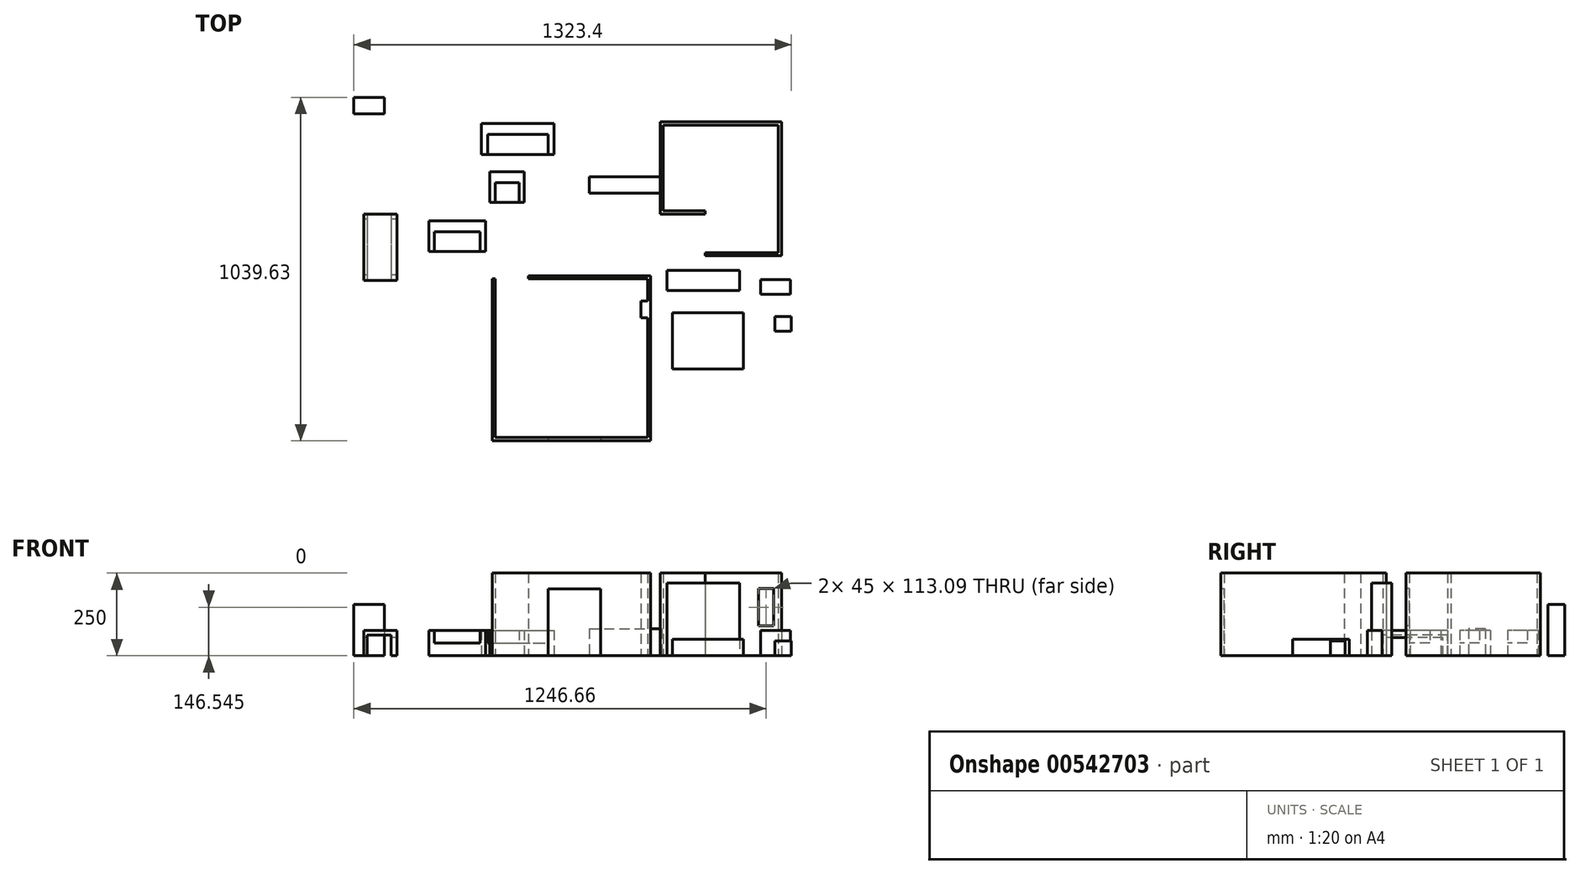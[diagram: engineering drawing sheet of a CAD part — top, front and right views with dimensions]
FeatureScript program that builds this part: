
annotation { "Feature Type Name" : "Feature", "Feature Type Description" : "" }
export const myFeature = defineFeature(function(context is Context, id is Id, definition is map)
    precondition{}
    {
        {
            var Q0;
            Q0=qCreatedBy(makeId("Top.planeOp"),FACE);
            var sketch = newSketch(context, id + "F0", { "sketchPlane" : qUnion([Q0])});
            skLineSegment(sketch, "E0", {"start": v(-41.59, 0) * mm, "end": v(-177.59, 0) * mm});
            skLineSegment(sketch, "E1", {"start": v(-177.59, 0) * mm, "end": v(-177.59, 280) * mm});
            skLineSegment(sketch, "E2", {"start": v(-177.59, 280) * mm, "end": v(190.41, 280) * mm});
            skLineSegment(sketch, "E3", {"start": v(190.41, 280) * mm, "end": v(190.41, -126) * mm});
            skLineSegment(sketch, "E4", {"start": v(190.41, -126) * mm, "end": v(-41.59, -126) * mm});
            skLineSegment(sketch, "E5", {"start": v(-41.59, -126) * mm, "end": v(-41.59, -101) * mm});
            skLineSegment(sketch, "E6", {"start": v(-41.59, -101) * mm, "end": v(-41.59, -101) * mm});
            skLineSegment(sketch, "E7", {"start": v(-41.59, -101) * mm, "end": v(-51.59, -101) * mm});
            skLineSegment(sketch, "E8", {"start": v(-41.59, -101) * mm, "end": v(-41.59, -116) * mm});
            skLineSegment(sketch, "E9", {"start": v(-41.59, -116) * mm, "end": v(180.41, -116) * mm});
            skLineSegment(sketch, "E10", {"start": v(180.41, -116) * mm, "end": v(180.41, 270) * mm});
            skLineSegment(sketch, "E11", {"start": v(180.41, 270) * mm, "end": v(-167.59, 270) * mm});
            skLineSegment(sketch, "E12", {"start": v(-167.59, 270) * mm, "end": v(-167.59, 10) * mm});
            skLineSegment(sketch, "E13", {"start": v(-167.59, 10) * mm, "end": v(-41.59, 10) * mm});
            skLineSegment(sketch, "E14", {"start": v(-41.59, 10) * mm, "end": v(-41.59, 0) * mm});
            skLineSegment(sketch, "E15", {"start": v(-51.59, -101) * mm, "end": v(-51.59, -126) * mm});
            skLineSegment(sketch, "E16", {"start": v(-51.59, -126) * mm, "end": v(-41.59, -126) * mm});
            skLineSegment(sketch, "E17", {"start": v(-575.48, -196) * mm, "end": v(-215.52, -196) * mm});
            skLineSegment(sketch, "E18", {"start": v(-215.52, -196) * mm, "end": v(-215.48, -263) * mm});
            skLineSegment(sketch, "E19", {"start": v(-215.48, -263) * mm, "end": v(-235.48, -263) * mm});
            skLineSegment(sketch, "E20", {"start": v(-235.48, -263) * mm, "end": v(-235.48, -313) * mm});
            skLineSegment(sketch, "E21", {"start": v(-235.48, -313) * mm, "end": v(-215.48, -313) * mm});
            skLineSegment(sketch, "E22", {"start": v(-215.48, -313) * mm, "end": v(-215.48, -676) * mm});
            skLineSegment(sketch, "E23", {"start": v(-215.48, -676) * mm, "end": v(-675.48, -676) * mm});
            skLineSegment(sketch, "E24", {"start": v(-675.48, -676) * mm, "end": v(-675.48, -196) * mm});
            skLineSegment(sketch, "E25", {"start": v(-675.48, -196) * mm, "end": v(-685.48, -196) * mm});
            skLineSegment(sketch, "E26", {"start": v(-685.48, -196) * mm, "end": v(-685.48, -686) * mm});
            skLineSegment(sketch, "E27", {"start": v(-685.48, -686) * mm, "end": v(-205.48, -686) * mm});
            skLineSegment(sketch, "E28", {"start": v(-205.48, -686) * mm, "end": v(-205.48, -186) * mm});
            skLineSegment(sketch, "E29", {"start": v(-205.48, -186) * mm, "end": v(-575.48, -186) * mm});
            skLineSegment(sketch, "E30", {"start": v(-575.48, -186) * mm, "end": v(-575.48, -196) * mm});
            skSolve(sketch);
        }
        {
            var Q0;
            Q0=makeQuery(id+"F0.imprint","IMPRINT",FACE,{"disambiguationData":[TD([[makeQuery(id+"F0.imprint","IMPRINT",EDGE,{"derivedFrom":sQuery(id+"F0.wireOp",EDGE,"E0")}),-1.0]])]});
            var Q1;
            Q1=makeQuery(id+"F0.imprint","IMPRINT",FACE,{"disambiguationData":[TD([[makeQuery(id+"F0.imprint","IMPRINT",EDGE,{"derivedFrom":sQuery(id+"F0.wireOp",EDGE,"E17")}),1.0]])]});
            extrude(context, id + "F1", {"entities" : qUnion([Q0, Q1]), "depth" : 250 * mm, "offsetDistance" : 25 * mm});
        }
        {
            var Q0;
            Q0=qCreatedBy(makeId("Top.planeOp"),FACE);
            var sketch = newSketch(context, id + "F2", { "sketchPlane" : qUnion([Q0])});
            skLineSegment(sketch, "E31.bottom", {"start": v(-156.32, -169.35) * mm, "end": v(63.68, -169.35) * mm});
            skLineSegment(sketch, "E31.top", {"start": v(-156.32, -230.35) * mm, "end": v(63.68, -230.35) * mm});
            skLineSegment(sketch, "E31.left", {"start": v(-156.32, -169.35) * mm, "end": v(-156.32, -230.35) * mm});
            skLineSegment(sketch, "E31.right", {"start": v(63.68, -169.35) * mm, "end": v(63.68, -230.35) * mm});
            skLineSegment(sketch, "E32.bottom", {"start": v(126.3, -197.85) * mm, "end": v(216.3, -197.85) * mm});
            skLineSegment(sketch, "E32.top", {"start": v(126.3, -242.85) * mm, "end": v(216.3, -242.85) * mm});
            skLineSegment(sketch, "E32.left", {"start": v(126.3, -197.85) * mm, "end": v(126.3, -242.85) * mm});
            skLineSegment(sketch, "E32.right", {"start": v(216.3, -197.85) * mm, "end": v(216.3, -242.85) * mm});
            skLineSegment(sketch, "E33.bottom", {"start": v(-139.85, -297.63) * mm, "end": v(74.15, -297.63) * mm});
            skLineSegment(sketch, "E33.top", {"start": v(-139.85, -468.63) * mm, "end": v(74.15, -468.63) * mm});
            skLineSegment(sketch, "E33.left", {"start": v(-139.85, -297.63) * mm, "end": v(-139.85, -468.63) * mm});
            skLineSegment(sketch, "E33.right", {"start": v(74.15, -297.63) * mm, "end": v(74.15, -468.63) * mm});
            skLineSegment(sketch, "E34.bottom", {"start": v(169.65, -309.64) * mm, "end": v(219.65, -309.64) * mm});
            skLineSegment(sketch, "E34.top", {"start": v(169.65, -354.64) * mm, "end": v(219.65, -354.64) * mm});
            skLineSegment(sketch, "E34.left", {"start": v(169.65, -309.64) * mm, "end": v(169.65, -354.64) * mm});
            skLineSegment(sketch, "E34.right", {"start": v(219.65, -309.64) * mm, "end": v(219.65, -354.64) * mm});
            skSolve(sketch);
        }
        {
            var Q0;
            Q0=makeQuery(id+"F2.imprint","IMPRINT",FACE,{"disambiguationData":[TD([[makeQuery(id+"F2.imprint","IMPRINT",EDGE,{"derivedFrom":sQuery(id+"F2.wireOp",EDGE,"E34.bottom")}),-1.0]])]});
            extrude(context, id + "F3", {"entities" : qUnion([Q0]), "depth" : 45 * mm, "offsetDistance" : 25 * mm});
        }
        {
            var Q0;
            Q0=makeQuery(id+"F2.imprint","IMPRINT",FACE,{"disambiguationData":[TD([[makeQuery(id+"F2.imprint","IMPRINT",EDGE,{"derivedFrom":sQuery(id+"F2.wireOp",EDGE,"E32.bottom")}),-1.0]])]});
            extrude(context, id + "F4", {"entities" : qUnion([Q0]), "depth" : 76 * mm, "offsetDistance" : 25 * mm});
        }
        {
            var Q0;
            Q0=makeQuery(id+"F2.imprint","IMPRINT",FACE,{"disambiguationData":[TD([[makeQuery(id+"F2.imprint","IMPRINT",EDGE,{"derivedFrom":sQuery(id+"F2.wireOp",EDGE,"E31.bottom")}),-1.0]])]});
            extrude(context, id + "F5", {"entities" : qUnion([Q0]), "depth" : 220 * mm, "offsetDistance" : 25 * mm});
        }
        {
            var Q0;
            Q0=makeQuery(id+"F2.imprint","IMPRINT",FACE,{"disambiguationData":[TD([[makeQuery(id+"F2.imprint","IMPRINT",EDGE,{"derivedFrom":sQuery(id+"F2.wireOp",EDGE,"E33.bottom")}),-1.0]])]});
            extrude(context, id + "F6", {"entities" : qUnion([Q0]), "depth" : 50 * mm, "offsetDistance" : 25 * mm});
        }
        {
            var Q0;
            Q0=qCreatedBy(makeId("Top.planeOp"),FACE);
            var sketch = newSketch(context, id + "F7", { "sketchPlane" : qUnion([Q0])});
            skLineSegment(sketch, "E35.bottom", {"start": v(-717.97, 274.17) * mm, "end": v(-497.97, 274.17) * mm});
            skLineSegment(sketch, "E35.top", {"start": v(-717.97, 181.17) * mm, "end": v(-497.97, 181.17) * mm});
            skLineSegment(sketch, "E35.left", {"start": v(-717.97, 274.17) * mm, "end": v(-717.97, 181.17) * mm});
            skLineSegment(sketch, "E35.right", {"start": v(-497.97, 274.17) * mm, "end": v(-497.97, 181.17) * mm});
            skLineSegment(sketch, "E36.bottom", {"start": v(-692.65, 129.05) * mm, "end": v(-588.65, 129.05) * mm});
            skLineSegment(sketch, "E36.top", {"start": v(-692.65, 36.05) * mm, "end": v(-588.65, 36.05) * mm});
            skLineSegment(sketch, "E36.left", {"start": v(-692.65, 129.05) * mm, "end": v(-692.65, 36.05) * mm});
            skLineSegment(sketch, "E36.right", {"start": v(-588.65, 129.05) * mm, "end": v(-588.65, 36.05) * mm});
            skLineSegment(sketch, "E37.bottom", {"start": v(-392.22, 113.71) * mm, "end": v(-172.22, 113.71) * mm});
            skLineSegment(sketch, "E37.top", {"start": v(-392.22, 63.71) * mm, "end": v(-172.22, 63.71) * mm});
            skLineSegment(sketch, "E37.left", {"start": v(-392.22, 113.71) * mm, "end": v(-392.22, 63.71) * mm});
            skLineSegment(sketch, "E37.right", {"start": v(-172.22, 113.71) * mm, "end": v(-172.22, 63.71) * mm});
            skLineSegment(sketch, "E38.bottom", {"start": v(-876.81, -20.43) * mm, "end": v(-705.81, -20.43) * mm});
            skLineSegment(sketch, "E38.top", {"start": v(-876.81, -113.43) * mm, "end": v(-705.81, -113.43) * mm});
            skLineSegment(sketch, "E38.left", {"start": v(-876.81, -20.43) * mm, "end": v(-876.81, -113.43) * mm});
            skLineSegment(sketch, "E38.right", {"start": v(-705.81, -20.43) * mm, "end": v(-705.81, -113.43) * mm});
            skLineSegment(sketch, "E39.bottom", {"start": v(-1073.3, 0) * mm, "end": v(-973.3, 0) * mm});
            skLineSegment(sketch, "E39.top", {"start": v(-1073.3, -200) * mm, "end": v(-973.3, -200) * mm});
            skLineSegment(sketch, "E39.left", {"start": v(-1073.3, 0) * mm, "end": v(-1073.3, -200) * mm});
            skLineSegment(sketch, "E39.right", {"start": v(-973.3, 0) * mm, "end": v(-973.3, -200) * mm});
            skLineSegment(sketch, "E40.bottom", {"start": v(-1103.75, 353.63) * mm, "end": v(-1010.75, 353.63) * mm});
            skLineSegment(sketch, "E40.top", {"start": v(-1103.75, 303.63) * mm, "end": v(-1010.75, 303.63) * mm});
            skLineSegment(sketch, "E40.left", {"start": v(-1103.75, 353.63) * mm, "end": v(-1103.75, 303.63) * mm});
            skLineSegment(sketch, "E40.right", {"start": v(-1010.75, 353.63) * mm, "end": v(-1010.75, 303.63) * mm});
            skSolve(sketch);
        }
        {
            var Q0;
            Q0=makeQuery(id+"F7.imprint","IMPRINT",FACE,{"disambiguationData":[TD([[makeQuery(id+"F7.imprint","IMPRINT",EDGE,{"derivedFrom":sQuery(id+"F7.wireOp",EDGE,"E35.bottom")}),-1.0]])]});
            var Q1;
            Q1=makeQuery(id+"F7.imprint","IMPRINT",FACE,{"disambiguationData":[TD([[makeQuery(id+"F7.imprint","IMPRINT",EDGE,{"derivedFrom":sQuery(id+"F7.wireOp",EDGE,"E36.bottom")}),-1.0]])]});
            var Q2;
            Q2=makeQuery(id+"F7.imprint","IMPRINT",FACE,{"disambiguationData":[TD([[makeQuery(id+"F7.imprint","IMPRINT",EDGE,{"derivedFrom":sQuery(id+"F7.wireOp",EDGE,"E38.bottom")}),-1.0]])]});
            extrude(context, id + "F8", {"entities" : qUnion([Q0, Q1, Q2]), "depth" : 77 * mm, "offsetDistance" : 25 * mm});
        }
        {
            var Q0;
            Q0=makeQuery(id+"F7.imprint","IMPRINT",FACE,{"disambiguationData":[TD([[makeQuery(id+"F7.imprint","IMPRINT",EDGE,{"derivedFrom":sQuery(id+"F7.wireOp",EDGE,"E37.bottom")}),-1.0]])]});
            extrude(context, id + "F9", {"entities" : qUnion([Q0]), "depth" : 81 * mm, "offsetDistance" : 25 * mm});
        }
        {
            var Q0;
            Q0=makeQuery(id+"F7.imprint","IMPRINT",FACE,{"disambiguationData":[TD([[makeQuery(id+"F7.imprint","IMPRINT",EDGE,{"derivedFrom":sQuery(id+"F7.wireOp",EDGE,"E39.bottom")}),-1.0]])]});
            extrude(context, id + "F10", {"entities" : qUnion([Q0]), "depth" : 77 * mm, "offsetDistance" : 25 * mm});
        }
        {
            var Q0;
            Q0=makeQuery(id+"F10.opExtrude","SWEPT_FACE",FACE,{"disambiguationData":[OSD([sQuery(id+"F7.wireOp",EDGE,"E39.left")])]});
            var sketch = newSketch(context, id + "F11", { "sketchPlane" : qUnion([Q0])});
            skLineSegment(sketch, "E41.bottom", {"start": v(14.46, 0) * mm, "end": v(184.22, 0) * mm});
            skLineSegment(sketch, "E41.top", {"start": v(14.46, 54.36) * mm, "end": v(184.22, 54.36) * mm});
            skLineSegment(sketch, "E41.left", {"start": v(14.46, 0) * mm, "end": v(14.46, 54.36) * mm});
            skLineSegment(sketch, "E41.right", {"start": v(184.22, 0) * mm, "end": v(184.22, 54.36) * mm});
            skSolve(sketch);
        }
        {
            var Q0;
            Q0 = qSketchRegion(id + "F11", true);
            var Q1;
            Q1=makeQuery(id+"F10.opExtrude","SWEPT_FACE",FACE,{"disambiguationData":[OSD([sQuery(id+"F7.wireOp",EDGE,"E39.right")])]});
            extrude(context, id + "F12", {"entities" : qUnion([Q0]), "operationType" : NewBodyOperationType.REMOVE, "endBound" : BoundingType.UP_TO_SURFACE, "oppositeDirection" : true, "depth" : 25 * mm, "endBoundEntityFace" : qUnion([Q1]), "offsetDistance" : 25 * mm});
        }
        {
            var Q0;
            Q0=makeQuery(id+"F7.imprint","IMPRINT",FACE,{"disambiguationData":[TD([[makeQuery(id+"F7.imprint","IMPRINT",EDGE,{"derivedFrom":sQuery(id+"F7.wireOp",EDGE,"E40.bottom")}),-1.0]])]});
            var Q1;
            Q1=sQuery(id+"F7.wireOp",EDGE,"E40.bottom");
            var Q2;
            Q2=sQuery(id+"F7.wireOp",EDGE,"E40.top");
            var Q3;
            Q3=sQuery(id+"F7.wireOp",EDGE,"E40.left");
            extrude(context, id + "F13", {"entities" : qUnion([Q0]), "surfaceEntities" : qUnion([Q1, Q2, Q3]), "depth" : 155 * mm, "offsetDistance" : 25 * mm});
        }
        {
            var Q0;
            Q0=makeQuery(id+"F10.opExtrude","SWEPT_FACE",FACE,{"disambiguationData":[OSD([sQuery(id+"F7.wireOp",EDGE,"E39.top")])]});
            var sketch = newSketch(context, id + "F14", { "sketchPlane" : qUnion([Q0])});
            skLineSegment(sketch, "E42.bottom", {"start": v(-1063.83, 0) * mm, "end": v(-990.86, 0) * mm});
            skLineSegment(sketch, "E42.top", {"start": v(-1063.83, 62.32) * mm, "end": v(-990.86, 62.32) * mm});
            skLineSegment(sketch, "E42.left", {"start": v(-1063.83, 0) * mm, "end": v(-1063.83, 62.32) * mm});
            skLineSegment(sketch, "E42.right", {"start": v(-990.86, 0) * mm, "end": v(-990.86, 62.32) * mm});
            skSolve(sketch);
        }
        {
            var Q0;
            Q0 = qSketchRegion(id + "F14", true);
            var Q1;
            Q1=makeQuery(id+"F10.opExtrude","SWEPT_FACE",FACE,{"disambiguationData":[OSD([sQuery(id+"F7.wireOp",EDGE,"E39.bottom")])]});
            extrude(context, id + "F15", {"entities" : qUnion([Q0]), "operationType" : NewBodyOperationType.REMOVE, "endBound" : BoundingType.UP_TO_SURFACE, "oppositeDirection" : true, "depth" : 25 * mm, "endBoundEntityFace" : qUnion([Q1]), "offsetDistance" : 25 * mm});
        }
        {
            var Q0;
            Q0=makeQuery(id+"F8.opExtrude","SWEPT_FACE",FACE,{"disambiguationData":[OSD([sQuery(id+"F7.wireOp",EDGE,"E38.top")])]});
            var sketch = newSketch(context, id + "F16", { "sketchPlane" : qUnion([Q0])});
            skPoint(sketch, "E43.oppositeSnap0", {"position": v(-705.81, 38.5) * mm});
            skLineSegment(sketch, "E43.bottom", {"start": v(-859.83, 77) * mm, "end": v(-721.64, 77) * mm});
            skLineSegment(sketch, "E43.top", {"start": v(-859.83, 38.5) * mm, "end": v(-721.64, 38.5) * mm});
            skLineSegment(sketch, "E43.left", {"start": v(-859.83, 77) * mm, "end": v(-859.83, 38.5) * mm});
            skLineSegment(sketch, "E43.right", {"start": v(-721.64, 77) * mm, "end": v(-721.64, 38.5) * mm});
            skSolve(sketch);
        }
        {
            var Q0;
            Q0 = qSketchRegion(id + "F16", true);
            extrude(context, id + "F17", {"entities" : qUnion([Q0]), "operationType" : NewBodyOperationType.REMOVE, "oppositeDirection" : true, "depth" : 60 * mm, "offsetDistance" : 25 * mm});
        }
        {
            var Q0;
            Q0=makeQuery(id+"F8.opExtrude","SWEPT_FACE",FACE,{"disambiguationData":[OSD([sQuery(id+"F7.wireOp",EDGE,"E36.top")])]});
            var sketch = newSketch(context, id + "F18", { "sketchPlane" : qUnion([Q0])});
            skPoint(sketch, "E44.oppositeSnap0", {"position": v(-588.65, 38.5) * mm});
            skLineSegment(sketch, "E44.bottom", {"start": v(-676.48, 77) * mm, "end": v(-603.08, 77) * mm});
            skLineSegment(sketch, "E44.top", {"start": v(-676.48, 38.5) * mm, "end": v(-603.08, 38.5) * mm});
            skLineSegment(sketch, "E44.left", {"start": v(-676.48, 77) * mm, "end": v(-676.48, 38.5) * mm});
            skLineSegment(sketch, "E44.right", {"start": v(-603.08, 77) * mm, "end": v(-603.08, 38.5) * mm});
            skSolve(sketch);
        }
        {
            var Q0;
            Q0 = qSketchRegion(id + "F18", true);
            extrude(context, id + "F19", {"entities" : qUnion([Q0]), "operationType" : NewBodyOperationType.REMOVE, "oppositeDirection" : true, "depth" : 60 * mm, "offsetDistance" : 25 * mm});
        }
        {
            var Q0;
            Q0=makeQuery(id+"F8.opExtrude","SWEPT_FACE",FACE,{"disambiguationData":[OSD([sQuery(id+"F7.wireOp",EDGE,"E35.top")])]});
            var sketch = newSketch(context, id + "F20", { "sketchPlane" : qUnion([Q0])});
            skPoint(sketch, "E45.oppositeSnap0", {"position": v(-497.97, 38.5) * mm});
            skLineSegment(sketch, "E45.bottom", {"start": v(-699.4, 77) * mm, "end": v(-516.02, 77) * mm});
            skLineSegment(sketch, "E45.top", {"start": v(-699.4, 38.5) * mm, "end": v(-516.02, 38.5) * mm});
            skLineSegment(sketch, "E45.left", {"start": v(-699.4, 77) * mm, "end": v(-699.4, 38.5) * mm});
            skLineSegment(sketch, "E45.right", {"start": v(-516.02, 77) * mm, "end": v(-516.02, 38.5) * mm});
            skSolve(sketch);
        }
        {
            var Q0;
            Q0 = qSketchRegion(id + "F20", true);
            extrude(context, id + "F21", {"entities" : qUnion([Q0]), "operationType" : NewBodyOperationType.REMOVE, "oppositeDirection" : true, "depth" : 60 * mm, "offsetDistance" : 25 * mm});
        }
        {
            var Q0;
            Q0=makeQuery(id+"F1.opExtrude","SWEPT_FACE",FACE,{"disambiguationData":[OSD([sQuery(id+"F0.wireOp",EDGE,"E27")])]});
            var sketch = newSketch(context, id + "F22", { "sketchPlane" : qUnion([Q0])});
            skLineSegment(sketch, "E46.bottom", {"start": v(-516.14, 0) * mm, "end": v(-357.3, 0) * mm});
            skLineSegment(sketch, "E46.top", {"start": v(-516.14, 202.24) * mm, "end": v(-357.3, 202.24) * mm});
            skLineSegment(sketch, "E46.left", {"start": v(-516.14, 0) * mm, "end": v(-516.14, 202.24) * mm});
            skLineSegment(sketch, "E46.right", {"start": v(-357.3, 0) * mm, "end": v(-357.3, 202.24) * mm});
            skSolve(sketch);
        }
        {
            var Q0;
            Q0 = qSketchRegion(id + "F22", true);
            extrude(context, id + "F23", {"entities" : qUnion([Q0]), "operationType" : NewBodyOperationType.REMOVE, "oppositeDirection" : true, "depth" : 25 * mm, "offsetDistance" : 25 * mm});
        }
        {
            var Q0;
            Q0=makeQuery(id+"F1.opExtrude","SWEPT_FACE",FACE,{"disambiguationData":[OSD([sQuery(id+"F0.wireOp",EDGE,"E4")])]});
            var sketch = newSketch(context, id + "F24", { "sketchPlane" : qUnion([Q0])});
            skLineSegment(sketch, "E47.bottom", {"start": v(165.41, 203.09) * mm, "end": v(120.41, 203.09) * mm});
            skLineSegment(sketch, "E47.top", {"start": v(165.41, 90) * mm, "end": v(120.41, 90) * mm});
            skLineSegment(sketch, "E47.left", {"start": v(165.41, 203.09) * mm, "end": v(165.41, 90) * mm});
            skLineSegment(sketch, "E47.right", {"start": v(120.41, 203.09) * mm, "end": v(120.41, 90) * mm});
            skSolve(sketch);
        }
        {
            var Q0;
            Q0 = qSketchRegion(id + "F24", true);
            extrude(context, id + "F25", {"entities" : qUnion([Q0]), "operationType" : NewBodyOperationType.REMOVE, "oppositeDirection" : true, "depth" : 25 * mm, "offsetDistance" : 25 * mm});
        }
    });
